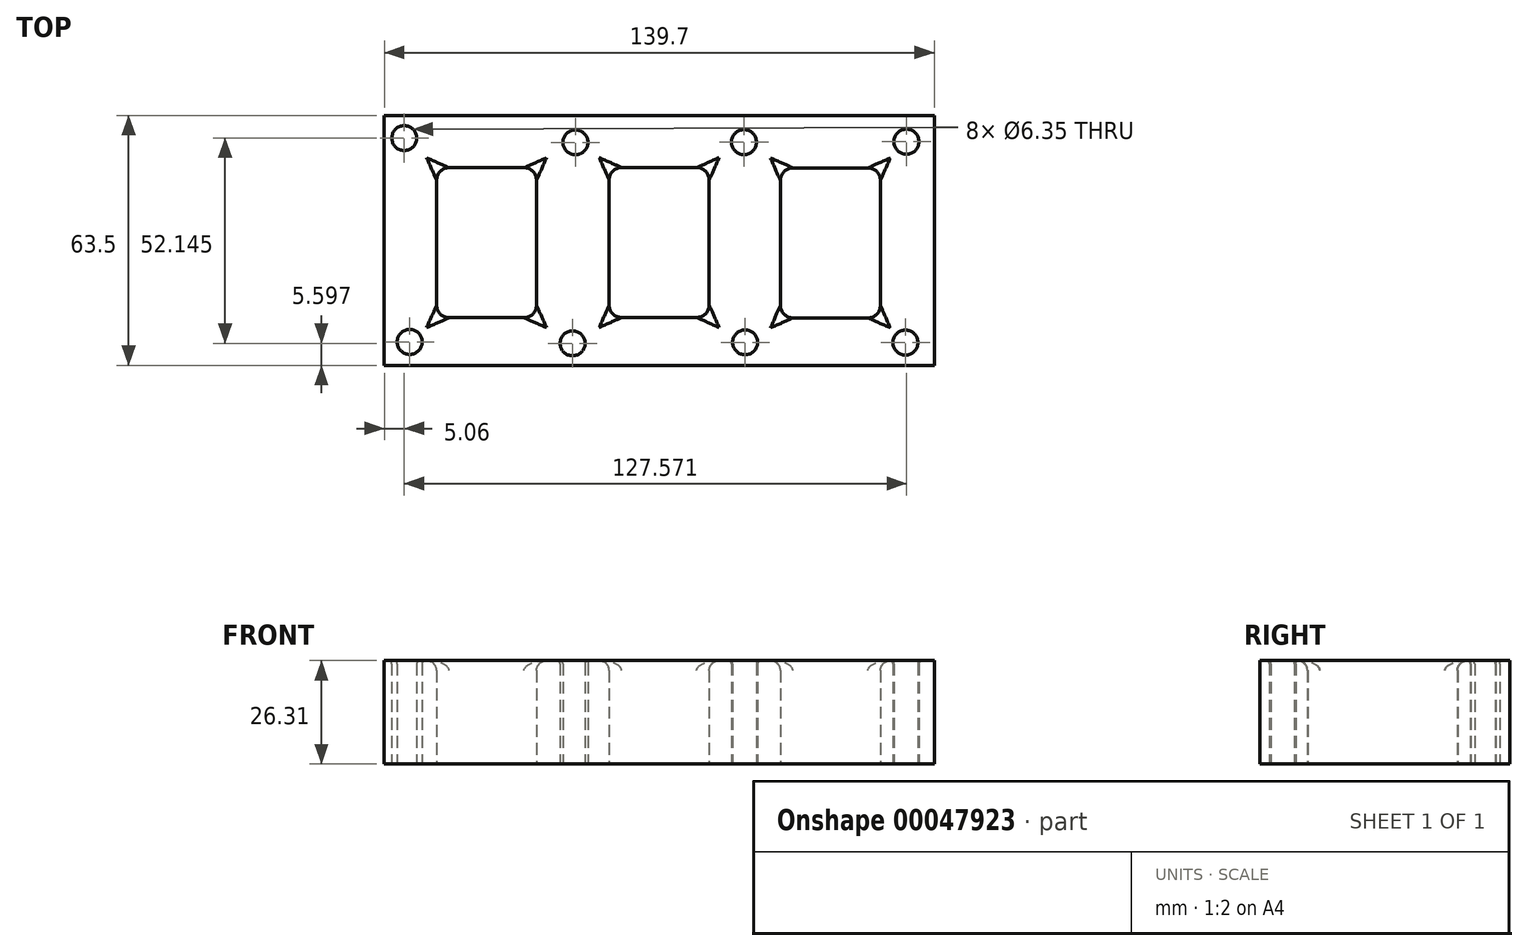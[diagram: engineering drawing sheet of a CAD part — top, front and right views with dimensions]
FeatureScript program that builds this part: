
annotation { "Feature Type Name" : "Feature", "Feature Type Description" : "" }
export const myFeature = defineFeature(function(context is Context, id is Id, definition is map)
    precondition{}
    {
        {
            var Q0;
            Q0=qCreatedBy(makeId("Top.planeOp"),FACE);
            var sketch = newSketch(context, id + "F0", { "sketchPlane" : qUnion([Q0])});
            skLineSegment(sketch, "E0.bottom", {"start": v(-68.08, 22.36) * mm, "end": v(71.62, 22.36) * mm});
            skLineSegment(sketch, "E0.top", {"start": v(-68.08, -41.14) * mm, "end": v(71.62, -41.14) * mm});
            skLineSegment(sketch, "E0.left", {"start": v(-68.08, 22.36) * mm, "end": v(-68.08, -41.14) * mm});
            skLineSegment(sketch, "E0.right", {"start": v(71.62, 22.36) * mm, "end": v(71.62, -41.14) * mm});
            skSolve(sketch);
        }
        {
            var Q0;
            Q0=qCreatedBy(makeId("Top.planeOp"),FACE);
            var sketch = newSketch(context, id + "F1", { "sketchPlane" : qUnion([Q0])});
            skLineSegment(sketch, "E1.bottom", {"start": v(-54.81, 9.07) * mm, "end": v(-29.41, 9.07) * mm});
            skLineSegment(sketch, "E1.top", {"start": v(-54.81, -29.03) * mm, "end": v(-29.41, -29.03) * mm});
            skLineSegment(sketch, "E1.left", {"start": v(-54.81, 9.07) * mm, "end": v(-54.81, -29.03) * mm});
            skLineSegment(sketch, "E1.right", {"start": v(-29.41, 9.07) * mm, "end": v(-29.41, -29.03) * mm});
            skLineSegment(sketch, "E2.bottom", {"start": v(-10.97, 9.11) * mm, "end": v(14.43, 9.11) * mm});
            skLineSegment(sketch, "E2.top", {"start": v(-10.97, -28.99) * mm, "end": v(14.43, -28.99) * mm});
            skLineSegment(sketch, "E2.left", {"start": v(-10.97, 9.11) * mm, "end": v(-10.97, -28.99) * mm});
            skLineSegment(sketch, "E2.right", {"start": v(14.43, 9.11) * mm, "end": v(14.43, -28.99) * mm});
            skLineSegment(sketch, "E3.bottom", {"start": v(32.54, 9.02) * mm, "end": v(57.94, 9.02) * mm});
            skLineSegment(sketch, "E3.top", {"start": v(32.54, -29.08) * mm, "end": v(57.94, -29.08) * mm});
            skLineSegment(sketch, "E3.left", {"start": v(32.54, 9.02) * mm, "end": v(32.54, -29.08) * mm});
            skLineSegment(sketch, "E3.right", {"start": v(57.94, 9.02) * mm, "end": v(57.94, -29.08) * mm});
            skSolve(sketch);
        }
        {
            var Q0;
            Q0=makeQuery(id+"F0.imprint","IMPRINT",FACE,{"disambiguationData":[TD([[makeQuery(id+"F0.imprint","IMPRINT",EDGE,{"derivedFrom":sQuery(id+"F0.wireOp",EDGE,"E0.bottom")}),-1.0]])]});
            extrude(context, id + "F2", {"entities" : qUnion([Q0]), "depth" : 26.3 * mm});
        }
        {
            var Q0;
            Q0=makeQuery(id+"F1.imprint","IMPRINT",FACE,{"disambiguationData":[TD([[makeQuery(id+"F1.imprint","IMPRINT",EDGE,{"derivedFrom":sQuery(id+"F1.wireOp",EDGE,"E1.bottom")}),-1.0]])]});
            var Q1;
            Q1=makeQuery(id+"F1.imprint","IMPRINT",FACE,{"disambiguationData":[TD([[makeQuery(id+"F1.imprint","IMPRINT",EDGE,{"derivedFrom":sQuery(id+"F1.wireOp",EDGE,"E2.bottom")}),-1.0]])]});
            var Q2;
            Q2=makeQuery(id+"F1.imprint","IMPRINT",FACE,{"disambiguationData":[TD([[makeQuery(id+"F1.imprint","IMPRINT",EDGE,{"derivedFrom":sQuery(id+"F1.wireOp",EDGE,"E3.bottom")}),-1.0]])]});
            extrude(context, id + "F3", {"entities" : qUnion([Q0, Q1, Q2]), "operationType" : NewBodyOperationType.REMOVE, "depth" : 77.6 * mm});
        }
        {
            var Q0;
            Q0=makeQuery(id+"F3.boolean.opBoolean","COPY",EDGE,{"derivedFrom":makeQuery(id+"F3.opExtrude","CAP_EDGE",EDGE,{"disambiguationData":[OSD([sQuery(id+"F1.wireOp",EDGE,"E1.top")])],"isStart":true})});
            var Q1;
            Q1=makeQuery(id+"F3.boolean.opBoolean","COPY",EDGE,{"derivedFrom":makeQuery(id+"F3.opExtrude","CAP_EDGE",EDGE,{"disambiguationData":[OSD([sQuery(id+"F1.wireOp",EDGE,"E1.right")])],"isStart":true})});
            var Q2;
            Q2=makeQuery(id+"F3.boolean.opBoolean","COPY",EDGE,{"derivedFrom":makeQuery(id+"F3.opExtrude","CAP_EDGE",EDGE,{"disambiguationData":[OSD([sQuery(id+"F1.wireOp",EDGE,"E1.bottom")])],"isStart":true})});
            var Q3;
            Q3=makeQuery(id+"F3.boolean.opBoolean","COPY",EDGE,{"derivedFrom":makeQuery(id+"F3.opExtrude","CAP_EDGE",EDGE,{"disambiguationData":[OSD([sQuery(id+"F1.wireOp",EDGE,"E1.left")])],"isStart":true})});
            var Q4;
            Q4=makeQuery(id+"F3.boolean.opBoolean","COPY",EDGE,{"derivedFrom":makeQuery(id+"F3.opExtrude","CAP_EDGE",EDGE,{"disambiguationData":[OSD([sQuery(id+"F1.wireOp",EDGE,"E2.left")])],"isStart":true})});
            var Q5;
            Q5=makeQuery(id+"F3.boolean.opBoolean","COPY",EDGE,{"derivedFrom":makeQuery(id+"F3.opExtrude","CAP_EDGE",EDGE,{"disambiguationData":[OSD([sQuery(id+"F1.wireOp",EDGE,"E2.top")])],"isStart":true})});
            var Q6;
            Q6=makeQuery(id+"F3.boolean.opBoolean","COPY",EDGE,{"derivedFrom":makeQuery(id+"F3.opExtrude","CAP_EDGE",EDGE,{"disambiguationData":[OSD([sQuery(id+"F1.wireOp",EDGE,"E2.right")])],"isStart":true})});
            var Q7;
            Q7=makeQuery(id+"F3.boolean.opBoolean","COPY",EDGE,{"derivedFrom":makeQuery(id+"F3.opExtrude","CAP_EDGE",EDGE,{"disambiguationData":[OSD([sQuery(id+"F1.wireOp",EDGE,"E2.bottom")])],"isStart":true})});
            var Q8;
            Q8=makeQuery(id+"F3.boolean.opBoolean","COPY",EDGE,{"derivedFrom":makeQuery(id+"F3.opExtrude","CAP_EDGE",EDGE,{"disambiguationData":[OSD([sQuery(id+"F1.wireOp",EDGE,"E3.left")])],"isStart":true})});
            var Q9;
            Q9=makeQuery(id+"F3.boolean.opBoolean","COPY",EDGE,{"derivedFrom":makeQuery(id+"F3.opExtrude","CAP_EDGE",EDGE,{"disambiguationData":[OSD([sQuery(id+"F1.wireOp",EDGE,"E3.bottom")])],"isStart":true})});
            var Q10;
            Q10=makeQuery(id+"F3.boolean.opBoolean","COPY",EDGE,{"derivedFrom":makeQuery(id+"F3.opExtrude","CAP_EDGE",EDGE,{"disambiguationData":[OSD([sQuery(id+"F1.wireOp",EDGE,"E3.right")])],"isStart":true})});
            var Q11;
            Q11=makeQuery(id+"F3.boolean.opBoolean","COPY",EDGE,{"derivedFrom":makeQuery(id+"F3.opExtrude","CAP_EDGE",EDGE,{"disambiguationData":[OSD([sQuery(id+"F1.wireOp",EDGE,"E3.top")])],"isStart":true})});
            var Q12;
            Q12=makeQuery(id+"F3.boolean.opBoolean","INTERSECT",EDGE,{"derivedFrom":[makeQuery(id+"F2.opExtrude","CAP_FACE",FACE,{"disambiguationData":[OSD([sQuery(id+"F0.wireOp",EDGE,"E0.bottom"),sQuery(id+"F0.wireOp",EDGE,"E0.top"),sQuery(id+"F0.wireOp",EDGE,"E0.left"),sQuery(id+"F0.wireOp",EDGE,"E0.right")])],"isStart":false}),makeQuery(id+"F3.opExtrude","SWEPT_FACE",FACE,{"disambiguationData":[OSD([sQuery(id+"F1.wireOp",EDGE,"E1.left")])]})]});
            var Q13;
            Q13=makeQuery(id+"F3.boolean.opBoolean","INTERSECT",EDGE,{"derivedFrom":[makeQuery(id+"F2.opExtrude","CAP_FACE",FACE,{"disambiguationData":[OSD([sQuery(id+"F0.wireOp",EDGE,"E0.bottom"),sQuery(id+"F0.wireOp",EDGE,"E0.top"),sQuery(id+"F0.wireOp",EDGE,"E0.left"),sQuery(id+"F0.wireOp",EDGE,"E0.right")])],"isStart":false}),makeQuery(id+"F3.opExtrude","SWEPT_FACE",FACE,{"disambiguationData":[OSD([sQuery(id+"F1.wireOp",EDGE,"E1.right")])]})]});
            var Q14;
            Q14=makeQuery(id+"F3.boolean.opBoolean","INTERSECT",EDGE,{"derivedFrom":[makeQuery(id+"F2.opExtrude","CAP_FACE",FACE,{"disambiguationData":[OSD([sQuery(id+"F0.wireOp",EDGE,"E0.bottom"),sQuery(id+"F0.wireOp",EDGE,"E0.top"),sQuery(id+"F0.wireOp",EDGE,"E0.left"),sQuery(id+"F0.wireOp",EDGE,"E0.right")])],"isStart":false}),makeQuery(id+"F3.opExtrude","SWEPT_FACE",FACE,{"disambiguationData":[OSD([sQuery(id+"F1.wireOp",EDGE,"E1.bottom")])]})]});
            var Q15;
            Q15=makeQuery(id+"F3.boolean.opBoolean","INTERSECT",EDGE,{"derivedFrom":[makeQuery(id+"F2.opExtrude","CAP_FACE",FACE,{"disambiguationData":[OSD([sQuery(id+"F0.wireOp",EDGE,"E0.bottom"),sQuery(id+"F0.wireOp",EDGE,"E0.top"),sQuery(id+"F0.wireOp",EDGE,"E0.left"),sQuery(id+"F0.wireOp",EDGE,"E0.right")])],"isStart":false}),makeQuery(id+"F3.opExtrude","SWEPT_FACE",FACE,{"disambiguationData":[OSD([sQuery(id+"F1.wireOp",EDGE,"E1.top")])]})]});
            var Q16;
            Q16=makeQuery(id+"F3.boolean.opBoolean","INTERSECT",EDGE,{"derivedFrom":[makeQuery(id+"F2.opExtrude","CAP_FACE",FACE,{"disambiguationData":[OSD([sQuery(id+"F0.wireOp",EDGE,"E0.bottom"),sQuery(id+"F0.wireOp",EDGE,"E0.top"),sQuery(id+"F0.wireOp",EDGE,"E0.left"),sQuery(id+"F0.wireOp",EDGE,"E0.right")])],"isStart":false}),makeQuery(id+"F3.opExtrude","SWEPT_FACE",FACE,{"disambiguationData":[OSD([sQuery(id+"F1.wireOp",EDGE,"E2.bottom")])]})]});
            var Q17;
            Q17=makeQuery(id+"F3.boolean.opBoolean","INTERSECT",EDGE,{"derivedFrom":[makeQuery(id+"F2.opExtrude","CAP_FACE",FACE,{"disambiguationData":[OSD([sQuery(id+"F0.wireOp",EDGE,"E0.bottom"),sQuery(id+"F0.wireOp",EDGE,"E0.top"),sQuery(id+"F0.wireOp",EDGE,"E0.left"),sQuery(id+"F0.wireOp",EDGE,"E0.right")])],"isStart":false}),makeQuery(id+"F3.opExtrude","SWEPT_FACE",FACE,{"disambiguationData":[OSD([sQuery(id+"F1.wireOp",EDGE,"E2.left")])]})]});
            var Q18;
            Q18=makeQuery(id+"F3.boolean.opBoolean","INTERSECT",EDGE,{"derivedFrom":[makeQuery(id+"F2.opExtrude","CAP_FACE",FACE,{"disambiguationData":[OSD([sQuery(id+"F0.wireOp",EDGE,"E0.bottom"),sQuery(id+"F0.wireOp",EDGE,"E0.top"),sQuery(id+"F0.wireOp",EDGE,"E0.left"),sQuery(id+"F0.wireOp",EDGE,"E0.right")])],"isStart":false}),makeQuery(id+"F3.opExtrude","SWEPT_FACE",FACE,{"disambiguationData":[OSD([sQuery(id+"F1.wireOp",EDGE,"E2.top")])]})]});
            var Q19;
            Q19=makeQuery(id+"F3.boolean.opBoolean","INTERSECT",EDGE,{"derivedFrom":[makeQuery(id+"F2.opExtrude","CAP_FACE",FACE,{"disambiguationData":[OSD([sQuery(id+"F0.wireOp",EDGE,"E0.bottom"),sQuery(id+"F0.wireOp",EDGE,"E0.top"),sQuery(id+"F0.wireOp",EDGE,"E0.left"),sQuery(id+"F0.wireOp",EDGE,"E0.right")])],"isStart":false}),makeQuery(id+"F3.opExtrude","SWEPT_FACE",FACE,{"disambiguationData":[OSD([sQuery(id+"F1.wireOp",EDGE,"E2.right")])]})]});
            var Q20;
            Q20=makeQuery(id+"F3.boolean.opBoolean","INTERSECT",EDGE,{"derivedFrom":[makeQuery(id+"F2.opExtrude","CAP_FACE",FACE,{"disambiguationData":[OSD([sQuery(id+"F0.wireOp",EDGE,"E0.bottom"),sQuery(id+"F0.wireOp",EDGE,"E0.top"),sQuery(id+"F0.wireOp",EDGE,"E0.left"),sQuery(id+"F0.wireOp",EDGE,"E0.right")])],"isStart":false}),makeQuery(id+"F3.opExtrude","SWEPT_FACE",FACE,{"disambiguationData":[OSD([sQuery(id+"F1.wireOp",EDGE,"E3.left")])]})]});
            var Q21;
            Q21=makeQuery(id+"F3.boolean.opBoolean","INTERSECT",EDGE,{"derivedFrom":[makeQuery(id+"F2.opExtrude","CAP_FACE",FACE,{"disambiguationData":[OSD([sQuery(id+"F0.wireOp",EDGE,"E0.bottom"),sQuery(id+"F0.wireOp",EDGE,"E0.top"),sQuery(id+"F0.wireOp",EDGE,"E0.left"),sQuery(id+"F0.wireOp",EDGE,"E0.right")])],"isStart":false}),makeQuery(id+"F3.opExtrude","SWEPT_FACE",FACE,{"disambiguationData":[OSD([sQuery(id+"F1.wireOp",EDGE,"E3.bottom")])]})]});
            var Q22;
            Q22=makeQuery(id+"F3.boolean.opBoolean","INTERSECT",EDGE,{"derivedFrom":[makeQuery(id+"F2.opExtrude","CAP_FACE",FACE,{"disambiguationData":[OSD([sQuery(id+"F0.wireOp",EDGE,"E0.bottom"),sQuery(id+"F0.wireOp",EDGE,"E0.top"),sQuery(id+"F0.wireOp",EDGE,"E0.left"),sQuery(id+"F0.wireOp",EDGE,"E0.right")])],"isStart":false}),makeQuery(id+"F3.opExtrude","SWEPT_FACE",FACE,{"disambiguationData":[OSD([sQuery(id+"F1.wireOp",EDGE,"E3.right")])]})]});
            var Q23;
            Q23=makeQuery(id+"F3.boolean.opBoolean","INTERSECT",EDGE,{"derivedFrom":[makeQuery(id+"F2.opExtrude","CAP_FACE",FACE,{"disambiguationData":[OSD([sQuery(id+"F0.wireOp",EDGE,"E0.bottom"),sQuery(id+"F0.wireOp",EDGE,"E0.top"),sQuery(id+"F0.wireOp",EDGE,"E0.left"),sQuery(id+"F0.wireOp",EDGE,"E0.right")])],"isStart":false}),makeQuery(id+"F3.opExtrude","SWEPT_FACE",FACE,{"disambiguationData":[OSD([sQuery(id+"F1.wireOp",EDGE,"E3.top")])]})]});
            fillet(context, id + "F4", {"entities" : qUnion([Q0, Q1, Q2, Q3, Q4, Q5, Q6, Q7, Q8, Q9, Q10, Q11, Q12, Q13, Q14, Q15, Q16, Q17, Q18, Q19, Q20, Q21, Q22, Q23]), "radius" : 2.54 * mm, "tangentPropagation" : true, "allowEdgeOverflow" : false});
        }
        {
            var Q0;
            Q0=makeQuery(id+"F3.boolean.opBoolean","COPY",EDGE,{"derivedFrom":makeQuery(id+"F3.opExtrude","SWEPT_EDGE",EDGE,{"disambiguationData":[OSD([sQuery(id+"F1.wireOp",EDGE,"E1.bottom"),sQuery(id+"F1.wireOp",EDGE,"E1.left")])]})});
            var Q1;
            Q1=makeQuery(id+"F3.boolean.opBoolean","COPY",EDGE,{"derivedFrom":makeQuery(id+"F3.opExtrude","SWEPT_EDGE",EDGE,{"disambiguationData":[OSD([sQuery(id+"F1.wireOp",EDGE,"E2.bottom"),sQuery(id+"F1.wireOp",EDGE,"E2.left")])]})});
            var Q2;
            Q2=makeQuery(id+"F3.boolean.opBoolean","COPY",EDGE,{"derivedFrom":makeQuery(id+"F3.opExtrude","SWEPT_EDGE",EDGE,{"disambiguationData":[OSD([sQuery(id+"F1.wireOp",EDGE,"E3.bottom"),sQuery(id+"F1.wireOp",EDGE,"E3.left")])]})});
            var Q3;
            Q3=makeQuery(id+"F3.boolean.opBoolean","COPY",EDGE,{"derivedFrom":makeQuery(id+"F3.opExtrude","SWEPT_EDGE",EDGE,{"disambiguationData":[OSD([sQuery(id+"F1.wireOp",EDGE,"E2.top"),sQuery(id+"F1.wireOp",EDGE,"E2.left")])]})});
            var Q4;
            Q4=makeQuery(id+"F3.boolean.opBoolean","COPY",EDGE,{"derivedFrom":makeQuery(id+"F3.opExtrude","SWEPT_EDGE",EDGE,{"disambiguationData":[OSD([sQuery(id+"F1.wireOp",EDGE,"E3.top"),sQuery(id+"F1.wireOp",EDGE,"E3.left")])]})});
            var Q5;
            Q5=makeQuery(id+"F3.boolean.opBoolean","COPY",EDGE,{"derivedFrom":makeQuery(id+"F3.opExtrude","SWEPT_EDGE",EDGE,{"disambiguationData":[OSD([sQuery(id+"F1.wireOp",EDGE,"E1.top"),sQuery(id+"F1.wireOp",EDGE,"E1.left")])]})});
            var Q6;
            Q6=makeQuery(id+"F3.boolean.opBoolean","COPY",EDGE,{"derivedFrom":makeQuery(id+"F3.opExtrude","SWEPT_EDGE",EDGE,{"disambiguationData":[OSD([sQuery(id+"F1.wireOp",EDGE,"E2.bottom"),sQuery(id+"F1.wireOp",EDGE,"E2.right")])]})});
            var Q7;
            Q7=makeQuery(id+"F3.boolean.opBoolean","COPY",EDGE,{"derivedFrom":makeQuery(id+"F3.opExtrude","SWEPT_EDGE",EDGE,{"disambiguationData":[OSD([sQuery(id+"F1.wireOp",EDGE,"E1.bottom"),sQuery(id+"F1.wireOp",EDGE,"E1.right")])]})});
            var Q8;
            Q8=makeQuery(id+"F3.boolean.opBoolean","COPY",EDGE,{"derivedFrom":makeQuery(id+"F3.opExtrude","SWEPT_EDGE",EDGE,{"disambiguationData":[OSD([sQuery(id+"F1.wireOp",EDGE,"E3.bottom"),sQuery(id+"F1.wireOp",EDGE,"E3.right")])]})});
            var Q9;
            Q9=makeQuery(id+"F3.boolean.opBoolean","COPY",EDGE,{"derivedFrom":makeQuery(id+"F3.opExtrude","SWEPT_EDGE",EDGE,{"disambiguationData":[OSD([sQuery(id+"F1.wireOp",EDGE,"E1.top"),sQuery(id+"F1.wireOp",EDGE,"E1.right")])]})});
            var Q10;
            Q10=makeQuery(id+"F3.boolean.opBoolean","COPY",EDGE,{"derivedFrom":makeQuery(id+"F3.opExtrude","SWEPT_EDGE",EDGE,{"disambiguationData":[OSD([sQuery(id+"F1.wireOp",EDGE,"E2.top"),sQuery(id+"F1.wireOp",EDGE,"E2.right")])]})});
            var Q11;
            Q11=makeQuery(id+"F3.boolean.opBoolean","COPY",EDGE,{"derivedFrom":makeQuery(id+"F3.opExtrude","SWEPT_EDGE",EDGE,{"disambiguationData":[OSD([sQuery(id+"F1.wireOp",EDGE,"E3.top"),sQuery(id+"F1.wireOp",EDGE,"E3.right")])]})});
            fillet(context, id + "F5", {"entities" : qUnion([Q0, Q1, Q2, Q3, Q4, Q5, Q6, Q7, Q8, Q9, Q10, Q11]), "radius" : 3.17 * mm, "tangentPropagation" : true, "allowEdgeOverflow" : false});
        }
        {
            var Q0;
            Q0=qCreatedBy(makeId("Top.planeOp"),FACE);
            var sketch = newSketch(context, id + "F6", { "sketchPlane" : qUnion([Q0])});
            skCircle(sketch, "E4", {"center": v(23.28, 15.58) * mm, "radius": 3.18 * mm});
            skCircle(sketch, "E5", {"center": v(-19.54, 15.52) * mm, "radius": 3.18 * mm});
            skCircle(sketch, "E6", {"center": v(-20.26, -35.54) * mm, "radius": 3.18 * mm});
            skCircle(sketch, "E7", {"center": v(23.59, -35.29) * mm, "radius": 3.18 * mm});
            skCircle(sketch, "E8", {"center": v(64.55, 15.68) * mm, "radius": 3.18 * mm});
            skCircle(sketch, "E9", {"center": v(64.3, -35.36) * mm, "radius": 3.18 * mm});
            skCircle(sketch, "E10", {"center": v(-61.64, -35.17) * mm, "radius": 3.18 * mm});
            skCircle(sketch, "E11", {"center": v(-63.02, 16.6) * mm, "radius": 3.18 * mm});
            skSolve(sketch);
        }
        {
            var Q0;
            Q0=makeQuery(id+"F6.imprint","IMPRINT",FACE,{"disambiguationData":[TD([[makeQuery(id+"F6.imprint","IMPRINT",EDGE,{"derivedFrom":sQuery(id+"F6.wireOp",EDGE,"E11")}),1.0]])]});
            var Q1;
            Q1=makeQuery(id+"F6.imprint","IMPRINT",FACE,{"disambiguationData":[TD([[makeQuery(id+"F6.imprint","IMPRINT",EDGE,{"derivedFrom":sQuery(id+"F6.wireOp",EDGE,"E10")}),1.0]])]});
            var Q2;
            Q2=makeQuery(id+"F6.imprint","IMPRINT",FACE,{"disambiguationData":[TD([[makeQuery(id+"F6.imprint","IMPRINT",EDGE,{"derivedFrom":sQuery(id+"F6.wireOp",EDGE,"E6")}),1.0]])]});
            var Q3;
            Q3=makeQuery(id+"F6.imprint","IMPRINT",FACE,{"disambiguationData":[TD([[makeQuery(id+"F6.imprint","IMPRINT",EDGE,{"derivedFrom":sQuery(id+"F6.wireOp",EDGE,"E5")}),1.0]])]});
            var Q4;
            Q4=makeQuery(id+"F6.imprint","IMPRINT",FACE,{"disambiguationData":[TD([[makeQuery(id+"F6.imprint","IMPRINT",EDGE,{"derivedFrom":sQuery(id+"F6.wireOp",EDGE,"E4")}),1.0]])]});
            var Q5;
            Q5=makeQuery(id+"F6.imprint","IMPRINT",FACE,{"disambiguationData":[TD([[makeQuery(id+"F6.imprint","IMPRINT",EDGE,{"derivedFrom":sQuery(id+"F6.wireOp",EDGE,"E8")}),1.0]])]});
            var Q6;
            Q6=makeQuery(id+"F6.imprint","IMPRINT",FACE,{"disambiguationData":[TD([[makeQuery(id+"F6.imprint","IMPRINT",EDGE,{"derivedFrom":sQuery(id+"F6.wireOp",EDGE,"E9")}),1.0]])]});
            var Q7;
            Q7=makeQuery(id+"F6.imprint","IMPRINT",FACE,{"disambiguationData":[TD([[makeQuery(id+"F6.imprint","IMPRINT",EDGE,{"derivedFrom":sQuery(id+"F6.wireOp",EDGE,"E7")}),1.0]])]});
            extrude(context, id + "F7", {"entities" : qUnion([Q0, Q1, Q2, Q3, Q4, Q5, Q6, Q7]), "operationType" : NewBodyOperationType.REMOVE, "depth" : 101.5 * mm});
        }
        {
            var Q0;
            Q0=makeQuery(id+"F7.boolean.opBoolean","COPY",EDGE,{"derivedFrom":makeQuery(id+"F7.opExtrude","CAP_EDGE",EDGE,{"disambiguationData":[OSD([sQuery(id+"F6.wireOp",EDGE,"E6")])],"isStart":true})});
            var Q1;
            Q1=makeQuery(id+"F7.boolean.opBoolean","COPY",EDGE,{"derivedFrom":makeQuery(id+"F7.opExtrude","CAP_EDGE",EDGE,{"disambiguationData":[OSD([sQuery(id+"F6.wireOp",EDGE,"E7")])],"isStart":true})});
            var Q2;
            Q2=makeQuery(id+"F7.boolean.opBoolean","COPY",EDGE,{"derivedFrom":makeQuery(id+"F7.opExtrude","CAP_EDGE",EDGE,{"disambiguationData":[OSD([sQuery(id+"F6.wireOp",EDGE,"E4")])],"isStart":true})});
            var Q3;
            Q3=makeQuery(id+"F7.boolean.opBoolean","COPY",EDGE,{"derivedFrom":makeQuery(id+"F7.opExtrude","CAP_EDGE",EDGE,{"disambiguationData":[OSD([sQuery(id+"F6.wireOp",EDGE,"E5")])],"isStart":true})});
            var Q4;
            Q4=makeQuery(id+"F7.boolean.opBoolean","COPY",EDGE,{"derivedFrom":makeQuery(id+"F7.opExtrude","CAP_EDGE",EDGE,{"disambiguationData":[OSD([sQuery(id+"F6.wireOp",EDGE,"E11")])],"isStart":true})});
            var Q5;
            Q5=makeQuery(id+"F7.boolean.opBoolean","COPY",EDGE,{"derivedFrom":makeQuery(id+"F7.opExtrude","CAP_EDGE",EDGE,{"disambiguationData":[OSD([sQuery(id+"F6.wireOp",EDGE,"E10")])],"isStart":true})});
            var Q6;
            Q6=makeQuery(id+"F7.boolean.opBoolean","COPY",EDGE,{"derivedFrom":makeQuery(id+"F7.opExtrude","CAP_EDGE",EDGE,{"disambiguationData":[OSD([sQuery(id+"F6.wireOp",EDGE,"E9")])],"isStart":true})});
            var Q7;
            Q7=makeQuery(id+"F7.boolean.opBoolean","COPY",EDGE,{"derivedFrom":makeQuery(id+"F7.opExtrude","CAP_EDGE",EDGE,{"disambiguationData":[OSD([sQuery(id+"F6.wireOp",EDGE,"E8")])],"isStart":true})});
            var Q8;
            Q8=makeQuery(id+"F7.boolean.opBoolean","INTERSECT",EDGE,{"derivedFrom":[makeQuery(id+"F2.opExtrude","CAP_FACE",FACE,{"disambiguationData":[OSD([sQuery(id+"F0.wireOp",EDGE,"E0.bottom"),sQuery(id+"F0.wireOp",EDGE,"E0.top"),sQuery(id+"F0.wireOp",EDGE,"E0.left"),sQuery(id+"F0.wireOp",EDGE,"E0.right")])],"isStart":false}),makeQuery(id+"F7.opExtrude","SWEPT_FACE",FACE,{"disambiguationData":[OSD([sQuery(id+"F6.wireOp",EDGE,"E6")])]})]});
            var Q9;
            Q9=makeQuery(id+"F7.boolean.opBoolean","INTERSECT",EDGE,{"derivedFrom":[makeQuery(id+"F2.opExtrude","CAP_FACE",FACE,{"disambiguationData":[OSD([sQuery(id+"F0.wireOp",EDGE,"E0.bottom"),sQuery(id+"F0.wireOp",EDGE,"E0.top"),sQuery(id+"F0.wireOp",EDGE,"E0.left"),sQuery(id+"F0.wireOp",EDGE,"E0.right")])],"isStart":false}),makeQuery(id+"F7.opExtrude","SWEPT_FACE",FACE,{"disambiguationData":[OSD([sQuery(id+"F6.wireOp",EDGE,"E10")])]})]});
            var Q10;
            Q10=makeQuery(id+"F7.boolean.opBoolean","INTERSECT",EDGE,{"derivedFrom":[makeQuery(id+"F2.opExtrude","CAP_FACE",FACE,{"disambiguationData":[OSD([sQuery(id+"F0.wireOp",EDGE,"E0.bottom"),sQuery(id+"F0.wireOp",EDGE,"E0.top"),sQuery(id+"F0.wireOp",EDGE,"E0.left"),sQuery(id+"F0.wireOp",EDGE,"E0.right")])],"isStart":false}),makeQuery(id+"F7.opExtrude","SWEPT_FACE",FACE,{"disambiguationData":[OSD([sQuery(id+"F6.wireOp",EDGE,"E7")])]})]});
            var Q11;
            Q11=makeQuery(id+"F7.boolean.opBoolean","INTERSECT",EDGE,{"derivedFrom":[makeQuery(id+"F2.opExtrude","CAP_FACE",FACE,{"disambiguationData":[OSD([sQuery(id+"F0.wireOp",EDGE,"E0.bottom"),sQuery(id+"F0.wireOp",EDGE,"E0.top"),sQuery(id+"F0.wireOp",EDGE,"E0.left"),sQuery(id+"F0.wireOp",EDGE,"E0.right")])],"isStart":false}),makeQuery(id+"F7.opExtrude","SWEPT_FACE",FACE,{"disambiguationData":[OSD([sQuery(id+"F6.wireOp",EDGE,"E9")])]})]});
            var Q12;
            Q12=makeQuery(id+"F7.boolean.opBoolean","INTERSECT",EDGE,{"derivedFrom":[makeQuery(id+"F2.opExtrude","CAP_FACE",FACE,{"disambiguationData":[OSD([sQuery(id+"F0.wireOp",EDGE,"E0.bottom"),sQuery(id+"F0.wireOp",EDGE,"E0.top"),sQuery(id+"F0.wireOp",EDGE,"E0.left"),sQuery(id+"F0.wireOp",EDGE,"E0.right")])],"isStart":false}),makeQuery(id+"F7.opExtrude","SWEPT_FACE",FACE,{"disambiguationData":[OSD([sQuery(id+"F6.wireOp",EDGE,"E8")])]})]});
            var Q13;
            Q13=makeQuery(id+"F7.boolean.opBoolean","INTERSECT",EDGE,{"derivedFrom":[makeQuery(id+"F2.opExtrude","CAP_FACE",FACE,{"disambiguationData":[OSD([sQuery(id+"F0.wireOp",EDGE,"E0.bottom"),sQuery(id+"F0.wireOp",EDGE,"E0.top"),sQuery(id+"F0.wireOp",EDGE,"E0.left"),sQuery(id+"F0.wireOp",EDGE,"E0.right")])],"isStart":false}),makeQuery(id+"F7.opExtrude","SWEPT_FACE",FACE,{"disambiguationData":[OSD([sQuery(id+"F6.wireOp",EDGE,"E4")])]})]});
            var Q14;
            Q14=makeQuery(id+"F7.boolean.opBoolean","INTERSECT",EDGE,{"derivedFrom":[makeQuery(id+"F2.opExtrude","CAP_FACE",FACE,{"disambiguationData":[OSD([sQuery(id+"F0.wireOp",EDGE,"E0.bottom"),sQuery(id+"F0.wireOp",EDGE,"E0.top"),sQuery(id+"F0.wireOp",EDGE,"E0.left"),sQuery(id+"F0.wireOp",EDGE,"E0.right")])],"isStart":false}),makeQuery(id+"F7.opExtrude","SWEPT_FACE",FACE,{"disambiguationData":[OSD([sQuery(id+"F6.wireOp",EDGE,"E5")])]})]});
            var Q15;
            Q15=makeQuery(id+"F7.boolean.opBoolean","INTERSECT",EDGE,{"derivedFrom":[makeQuery(id+"F2.opExtrude","CAP_FACE",FACE,{"disambiguationData":[OSD([sQuery(id+"F0.wireOp",EDGE,"E0.bottom"),sQuery(id+"F0.wireOp",EDGE,"E0.top"),sQuery(id+"F0.wireOp",EDGE,"E0.left"),sQuery(id+"F0.wireOp",EDGE,"E0.right")])],"isStart":false}),makeQuery(id+"F7.opExtrude","SWEPT_FACE",FACE,{"disambiguationData":[OSD([sQuery(id+"F6.wireOp",EDGE,"E11")])]})]});
            fillet(context, id + "F8", {"entities" : qUnion([Q0, Q1, Q2, Q3, Q4, Q5, Q6, Q7, Q8, Q9, Q10, Q11, Q12, Q13, Q14, Q15]), "radius" : 0.8 * mm, "tangentPropagation" : true, "allowEdgeOverflow" : false});
        }
    });
